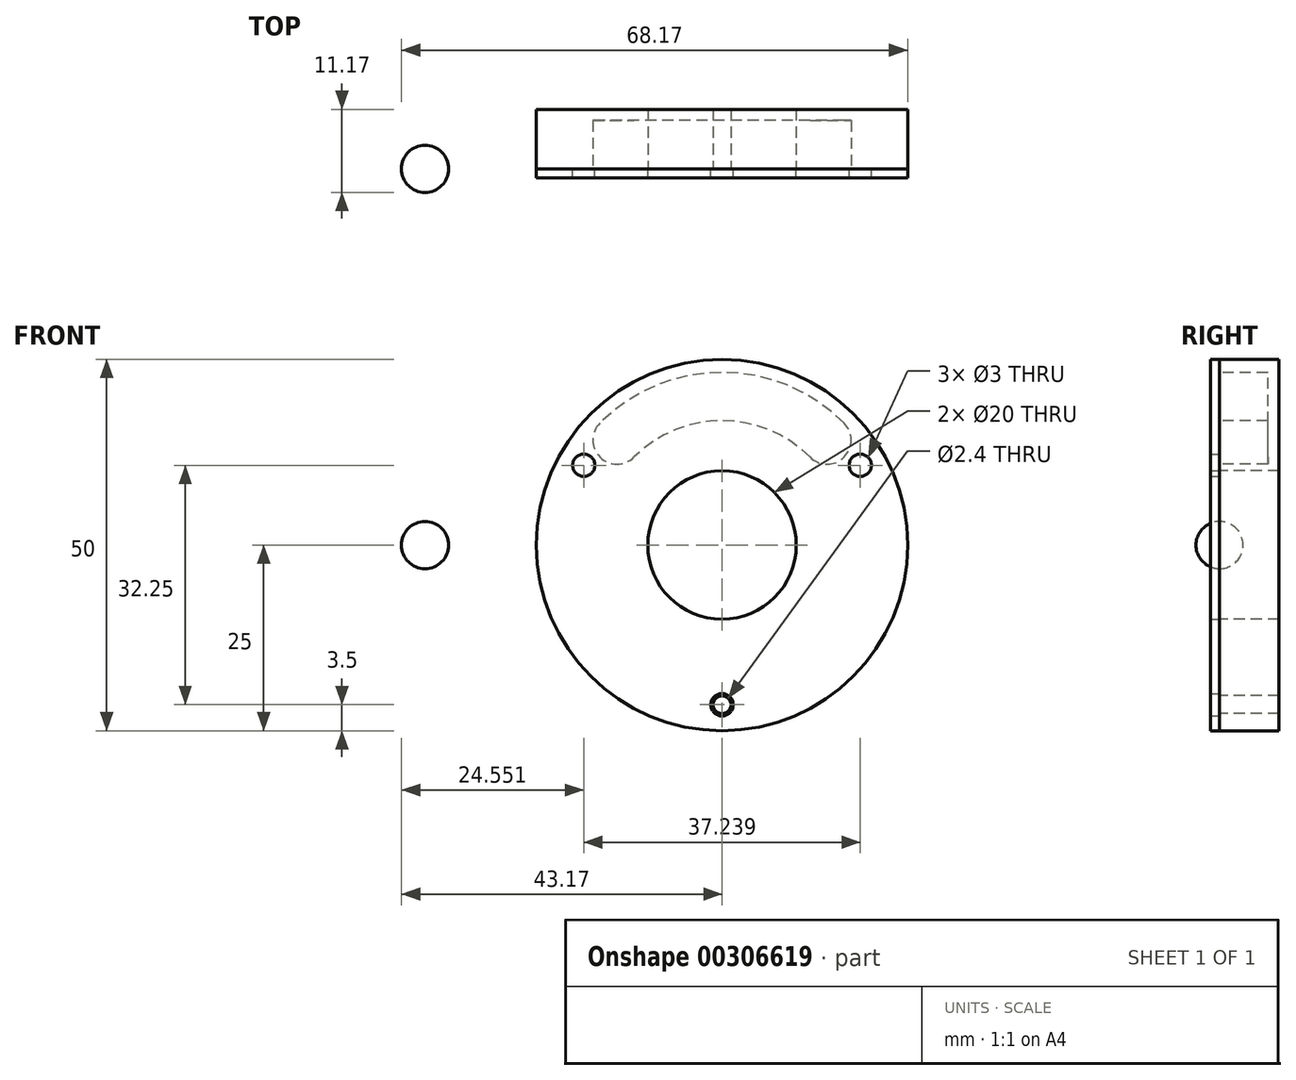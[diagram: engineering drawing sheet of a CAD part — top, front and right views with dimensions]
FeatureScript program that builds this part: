
annotation { "Feature Type Name" : "Feature", "Feature Type Description" : "" }
export const myFeature = defineFeature(function(context is Context, id is Id, definition is map)
    precondition{}
    {
        {
            var Q0;
            Q0=qCreatedBy(makeId("Front.planeOp"),FACE);
            var sketch = newSketch(context, id + "F0", { "sketchPlane" : qUnion([Q0])});
            skCircle(sketch, "E0", {"center": v(0, 0) * mm, "radius": 25 * mm});
            skCircle(sketch, "E1", {"center": v(0, 0) * mm, "radius": 10 * mm});
            skSolve(sketch);
        }
        {
            var Q0;
            Q0=qSketchRegion(id+"F0",true);
            extrude(context, id + "F1", {"entities" : qUnion([Q0]), "oppositeDirection" : true, "depth" : 8 * mm});
        }
        {
            var Q0;
            Q0=makeQuery(id+"F1.opExtrude","CAP_FACE",FACE,{"disambiguationData":[OSD([sQuery(id+"F0.wireOp",EDGE,"E0"),sQuery(id+"F0.wireOp",EDGE,"E1")])],"isStart":true});
            var sketch = newSketch(context, id + "F2", { "sketchPlane" : qUnion([Q0])});
            skArc(sketch, "E2", {"start": v(-14.14, 14.14) * mm, "mid": v(0, 20) * mm, "end": v(14.14, 14.14) * mm, "construction": true});
            skLineSegment(sketch, "E3", {"start": v(0, 0) * mm, "end": v(0, 25) * mm, "construction": true});
            skPoint(sketch, "E3.endSnap0", {"position": v(0, 20) * mm});
            skLineSegment(sketch, "E4", {"start": v(-14.14, 14.14) * mm, "end": v(0, 0) * mm, "construction": true});
            skArc(sketch, "E5.0.startCap", {"start": v(-11.84, 11.84) * mm, "mid": v(-16.44, 11.84) * mm, "end": v(-16.44, 16.44) * mm});
            skArc(sketch, "E5.0.endCap", {"start": v(16.44, 16.44) * mm, "mid": v(16.44, 11.84) * mm, "end": v(11.84, 11.84) * mm});
            skArc(sketch, "E5.0.left", {"start": v(-16.44, 16.44) * mm, "mid": v(0, 23.25) * mm, "end": v(16.44, 16.44) * mm});
            skArc(sketch, "E5.0.right", {"start": v(-11.84, 11.84) * mm, "mid": v(0, 16.75) * mm, "end": v(11.84, 11.84) * mm});
            skSolve(sketch);
        }
        {
            var Q0;
            Q0=qSketchRegion(id+"F2",true);
            extrude(context, id + "F3", {"entities" : qUnion([Q0]), "operationType" : NewBodyOperationType.REMOVE, "oppositeDirection" : true, "depth" : 6.5 * mm});
        }
        {
            var Q0;
            Q0=makeQuery(id+"F1.opExtrude","CAP_FACE",FACE,{"disambiguationData":[OSD([sQuery(id+"F0.wireOp",EDGE,"E0"),sQuery(id+"F0.wireOp",EDGE,"E1")])],"isStart":true});
            var sketch = newSketch(context, id + "F4", { "sketchPlane" : qUnion([Q0])});
            skPoint(sketch, "E6", {"position": v(0, -21.5) * mm});
            skSolve(sketch);
        }
        {
            var Q0;
            Q0=sQuery(id+"F4.wireOp",VERTEX,"E6");
            var Q1;
            Q1=makeQuery(id+"F1.opExtrude","SWEPT_BODY",BODY,{"disambiguationData":[OSD([sQuery(id+"F0.wireOp",EDGE,"E0"),sQuery(id+"F0.wireOp",EDGE,"E1")])]});
            hole(context, id + "F5", {"style" : HoleStyle.SIMPLE, "endStyle" : HoleEndStyle.THROUGH, "standardTappedOrClearance" : lookupTablePath({ "standard" : "ISO", "engagement" : "75%", "pitch" : "0.6 mm", "size" : "M3", "type" : "Tapped" }), "standardBlindInLast" : lookupTablePath({ "standard" : "ISO", "engagement" : "75%", "pitch" : "0.6 mm", "size" : "M3", "type" : "Tapped" }), "holeDiameter" : 2.4 * mm, "showTappedDepth" : true, "tappedDepth" : 6 * mm, "tapClearance" : 2, "locations" : qUnion([Q0]), "scope" : qUnion([Q1])});
        }
        {
            var Q0;
            Q0=makeQuery(id+"F1.opExtrude","CAP_FACE",FACE,{"disambiguationData":[OSD([sQuery(id+"F0.wireOp",EDGE,"E0"),sQuery(id+"F0.wireOp",EDGE,"E1")])],"isStart":true});
            var sketch = newSketch(context, id + "F6", { "sketchPlane" : qUnion([Q0])});
            skCircle(sketch, "E7", {"center": v(0, 0) * mm, "radius": 25 * mm});
            skCircle(sketch, "E8", {"center": v(-18.62, 10.75) * mm, "radius": 1.5 * mm});
            skCircle(sketch, "E9", {"center": v(18.62, 10.75) * mm, "radius": 1.5 * mm});
            skCircle(sketch, "E10", {"center": v(0, -21.5) * mm, "radius": 1.5 * mm});
            skCircle(sketch, "E11", {"center": v(0, 0) * mm, "radius": 10 * mm});
            skSolve(sketch);
        }
        {
            var Q0;
            Q0=qSketchRegion(id+"F6",true);
            extrude(context, id + "F7", {"entities" : qUnion([Q0]), "depth" : 1.2 * mm});
        }
        {
            var Q0;
            Q0=qCreatedBy(makeId("Front.planeOp"),FACE);
            var sketch = newSketch(context, id + "F8", { "sketchPlane" : qUnion([Q0])});
            skArc(sketch, "E12", {"start": v(-36.83, 0) * mm, "mid": v(-40, 3.17) * mm, "end": v(-43.17, 0) * mm});
            skLineSegment(sketch, "E13", {"start": v(-43.17, 0) * mm, "end": v(-36.83, 0) * mm});
            skSolve(sketch);
        }
        {
            var Q0;
            Q0=makeQuery(id+"F8.imprint","IMPRINT",FACE,{"disambiguationData":[TD([[makeQuery(id+"F8.imprint","IMPRINT",EDGE,{"derivedFrom":sQuery(id+"F8.wireOp",EDGE,"E12")}),1.0]])]});
            var Q1;
            Q1=sQuery(id+"F8.wireOp",EDGE,"E12");
            var Q2;
            Q2=sQuery(id+"F8.wireOp",EDGE,"E13");
            revolve(context, id + "F9", {"entities" : qUnion([Q0]), "surfaceEntities" : qUnion([Q1]), "axis" : qUnion([Q2]), "revolveType" : RevolveType.FULL});
        }
    });
